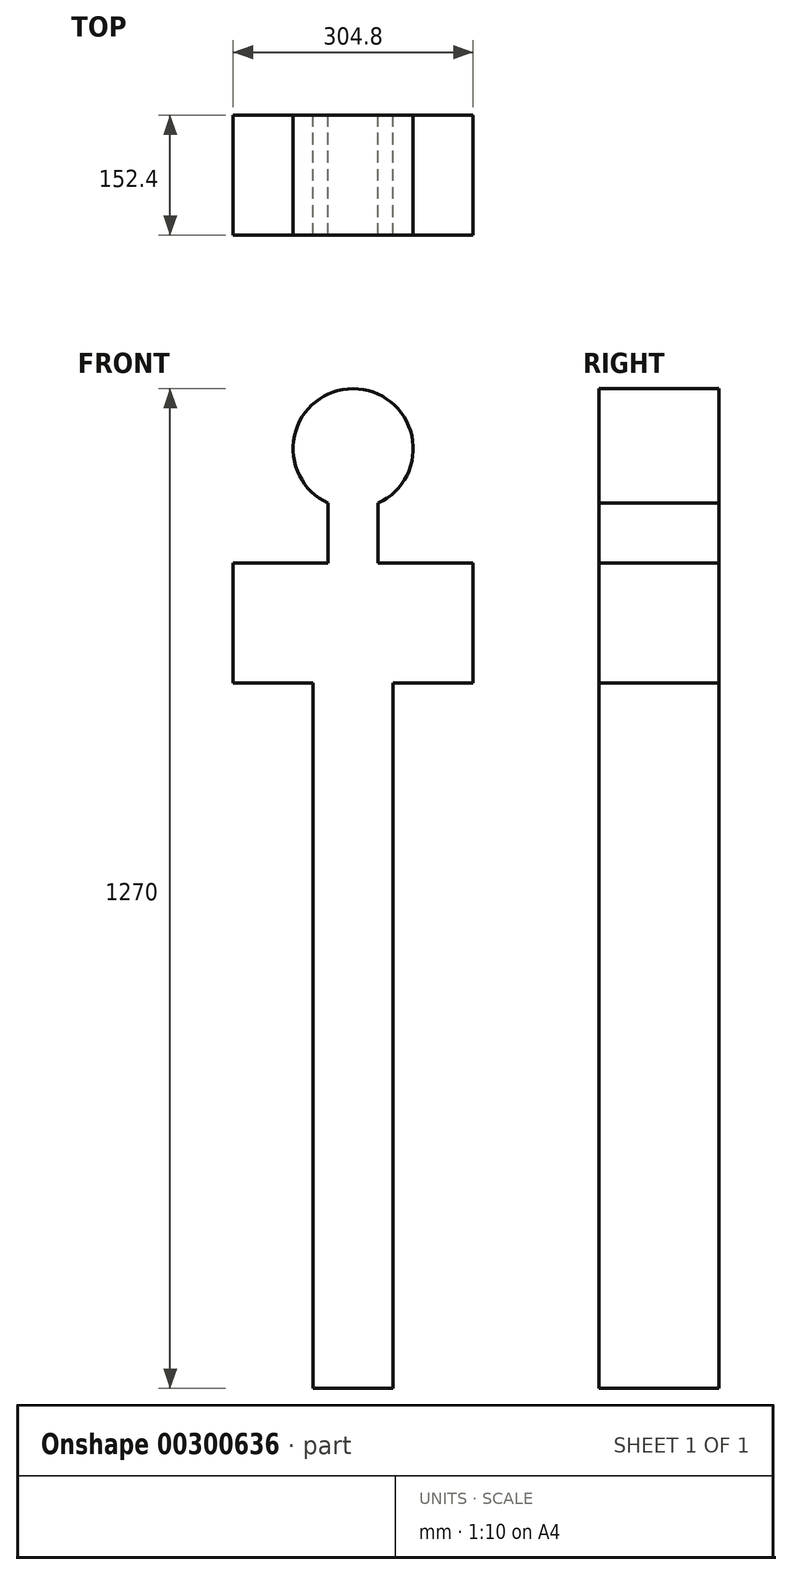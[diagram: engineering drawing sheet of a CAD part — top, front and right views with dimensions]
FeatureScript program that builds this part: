
annotation { "Feature Type Name" : "Feature", "Feature Type Description" : "" }
export const myFeature = defineFeature(function(context is Context, id is Id, definition is map)
    precondition{}
    {
        {
            var Q0;
            Q0=qCreatedBy(makeId("Front.planeOp"),FACE);
            var sketch = newSketch(context, id + "F0", { "sketchPlane" : qUnion([Q0])});
            skArc(sketch, "E0", {"start": v(31.75, -69.27) * mm, "mid": v(0, 76.2) * mm, "end": v(-31.75, -69.27) * mm});
            skLineSegment(sketch, "E1", {"start": v(-31.75, -145.62) * mm, "end": v(-152.4, -145.62) * mm});
            skLineSegment(sketch, "E2", {"start": v(-152.4, -145.62) * mm, "end": v(-152.4, -298.02) * mm});
            skLineSegment(sketch, "E3", {"start": v(-152.4, -298.02) * mm, "end": v(-50.8, -298.02) * mm});
            skLineSegment(sketch, "E4", {"start": v(-50.8, -298.02) * mm, "end": v(-50.8, -1193.8) * mm});
            skLineSegment(sketch, "E5", {"start": v(-50.8, -1193.8) * mm, "end": v(50.8, -1193.8) * mm});
            skLineSegment(sketch, "E6", {"start": v(50.8, -1193.8) * mm, "end": v(50.8, -298.02) * mm});
            skLineSegment(sketch, "E7", {"start": v(50.8, -298.02) * mm, "end": v(152.4, -298.02) * mm});
            skLineSegment(sketch, "E8", {"start": v(152.4, -298.02) * mm, "end": v(152.4, -145.62) * mm});
            skLineSegment(sketch, "E9", {"start": v(152.4, -145.62) * mm, "end": v(31.75, -145.62) * mm});
            skLineSegment(sketch, "E10", {"start": v(-31.75, -145.62) * mm, "end": v(-31.75, -69.27) * mm});
            skLineSegment(sketch, "E11", {"start": v(31.75, -145.62) * mm, "end": v(31.75, -69.27) * mm});
            skSolve(sketch);
        }
        {
            var Q0;
            Q0 = qSketchRegion(id + "F0", true);
            extrude(context, id + "F1", {"entities" : qUnion([Q0]), "depth" : 152.4 * mm});
        }
    });
